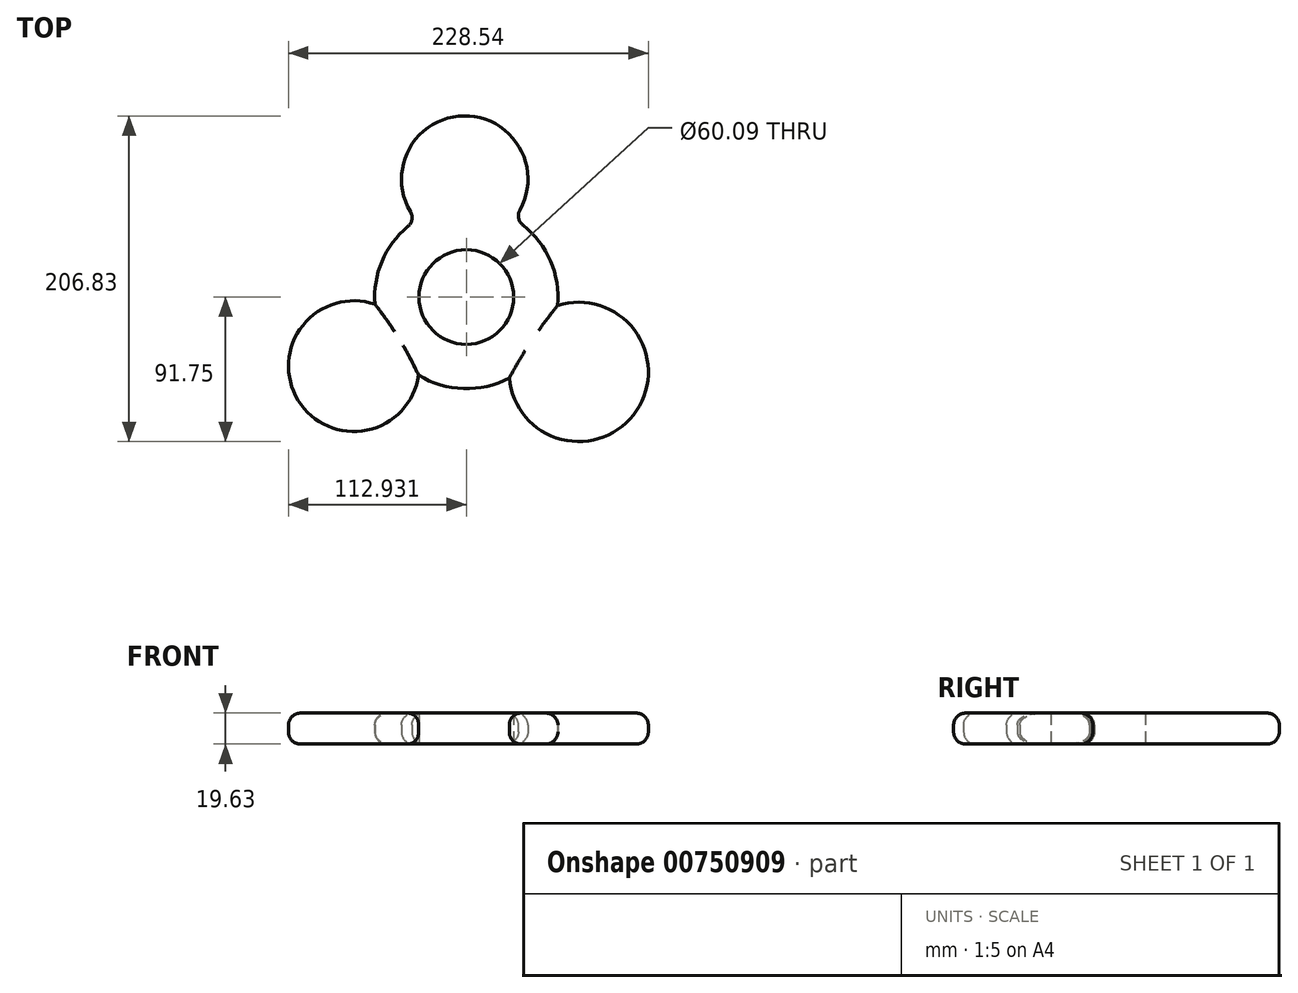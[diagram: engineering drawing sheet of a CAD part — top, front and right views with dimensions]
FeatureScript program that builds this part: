
annotation { "Feature Type Name" : "Feature", "Feature Type Description" : "" }
export const myFeature = defineFeature(function(context is Context, id is Id, definition is map)
    precondition{}
    {
        {
            var Q0;
            Q0=qCreatedBy(makeId("Top.planeOp"),FACE);
            var sketch = newSketch(context, id + "F0", { "sketchPlane" : qUnion([Q0])});
            skCircle(sketch, "E0", {"center": v(5.2, 0) * mm, "radius": 30.04 * mm});
            skCircle(sketch, "E1", {"center": v(5.2, 0) * mm, "radius": 58.18 * mm});
            skSolve(sketch);
        }
        {
            var Q0;
            Q0 = qSketchRegion(id + "F0", true);
            extrude(context, id + "F1", {"entities" : qUnion([Q0]), "depth" : 6.93 * mm, "offsetDistance" : 25.4 * mm});
        }
        {
            var Q0;
            Q0=qCreatedBy(makeId("Top.planeOp"),FACE);
            var sketch = newSketch(context, id + "F2", { "sketchPlane" : qUnion([Q0])});
            skCircle(sketch, "E2", {"center": v(4.18, 74.93) * mm, "radius": 40.15 * mm});
            skCircle(sketch, "E3", {"center": v(-66.22, -43.86) * mm, "radius": 41.52 * mm});
            skCircle(sketch, "E4", {"center": v(76.59, -47.53) * mm, "radius": 44.23 * mm});
            skSolve(sketch);
        }
        {
            var Q0;
            Q0 = qSketchRegion(id + "F2", true);
            extrude(context, id + "F3", {"entities" : qUnion([Q0]), "operationType" : NewBodyOperationType.ADD, "depth" : 6.93 * mm, "offsetDistance" : 25.4 * mm});
        }
        {
            var Q0;
            Q0=makeQuery(id+"F3.boolean.opBoolean","MERGE",FACE,{"derivedFrom":[makeQuery(id+"F1.opExtrude","CAP_FACE",FACE,{"disambiguationData":[OSD([sQuery(id+"F0.wireOp",EDGE,"E0"),sQuery(id+"F0.wireOp",EDGE,"E1")])],"isStart":false}),makeQuery(id+"F3.opExtrude","CAP_FACE",FACE,{"disambiguationData":[OSD([sQuery(id+"F2.wireOp",EDGE,"E2"),sQuery(id+"F2.wireOp",EDGE,"RJi2fS6J-4N5A-JJYD-STQZ-maYoIMxHux2H")])],"isStart":false}),makeQuery(id+"F3.opExtrude","CAP_FACE",FACE,{"disambiguationData":[OSD([sQuery(id+"F2.wireOp",EDGE,"E3"),sQuery(id+"F2.wireOp",EDGE,"9FHdYVCZ-X2J7-zCW8-irfW-GTTB5p2rgJZV")])],"isStart":false}),makeQuery(id+"F3.opExtrude","CAP_FACE",FACE,{"disambiguationData":[OSD([sQuery(id+"F2.wireOp",EDGE,"E4"),sQuery(id+"F2.wireOp",EDGE,"hhuE4voa-zWzk-uKp9-sCeD-eiZH0AJFDme7")])],"isStart":false})]});
            extrude(context, id + "F4", {"entities" : qUnion([Q0]), "operationType" : NewBodyOperationType.ADD, "depth" : 12.7 * mm, "offsetDistance" : 25.4 * mm});
        }
        {
            var Q0;
            {var subQ0=sQuery(id+"F2.wireOp",EDGE,"E3");var subQ1=sQuery(id+"F0.wireOp",EDGE,"E1");var subQ2=sQuery(id+"F2.wireOp",EDGE,"E4");Q0=makeQuery(id+"F4.opExtrude","CAP_EDGE",EDGE,{"disambiguationData":[OSD([subQ1]),TDD([makeQuery(id+"F3.boolean.opBoolean","SPLIT",EDGE,{"disambiguationData":[TD([makeQuery(id+"F1.opExtrude","CAP_FACE",FACE,{"disambiguationData":[OSD([sQuery(id+"F0.wireOp",EDGE,"E0"),subQ1])],"isStart":false}),makeQuery(id+"F1.opExtrude","SWEPT_FACE",FACE,{"disambiguationData":[OSD([subQ1])]}),makeQuery(id+"F3.opExtrude","CAP_FACE",FACE,{"disambiguationData":[OSD([sQuery(id+"F2.wireOp",EDGE,"E2"),sQuery(id+"F2.wireOp",EDGE,"RJi2fS6J-4N5A-JJYD-STQZ-maYoIMxHux2H")])],"isStart":false}),makeQuery(id+"F3.opExtrude","SWEPT_FACE",FACE,{"disambiguationData":[OSD([subQ0])]}),makeQuery(id+"F3.opExtrude","CAP_FACE",FACE,{"disambiguationData":[OSD([subQ0,sQuery(id+"F2.wireOp",EDGE,"9FHdYVCZ-X2J7-zCW8-irfW-GTTB5p2rgJZV")])],"isStart":false}),makeQuery(id+"F3.opExtrude","SWEPT_FACE",FACE,{"disambiguationData":[OSD([subQ2])]}),makeQuery(id+"F3.opExtrude","CAP_FACE",FACE,{"disambiguationData":[OSD([subQ2,sQuery(id+"F2.wireOp",EDGE,"hhuE4voa-zWzk-uKp9-sCeD-eiZH0AJFDme7")])],"isStart":false})])],"derivedFrom":makeQuery(id+"F1.opExtrude","CAP_EDGE",EDGE,{"disambiguationData":[OSD([subQ1])],"isStart":false})})])],"isStart":false});}
            var Q1;
            {var subQ0=sQuery(id+"F0.wireOp",EDGE,"E1");var subQ1=sQuery(id+"F2.wireOp",EDGE,"E3");var subQ2=sQuery(id+"F2.wireOp",EDGE,"E4");Q1=makeQuery(id+"F3.boolean.opBoolean","SPLIT",EDGE,{"disambiguationData":[TD([makeQuery(id+"F1.opExtrude","CAP_FACE",FACE,{"disambiguationData":[OSD([sQuery(id+"F0.wireOp",EDGE,"E0"),subQ0])],"isStart":true}),makeQuery(id+"F1.opExtrude","SWEPT_FACE",FACE,{"disambiguationData":[OSD([subQ0])]}),makeQuery(id+"F3.opExtrude","CAP_FACE",FACE,{"disambiguationData":[OSD([sQuery(id+"F2.wireOp",EDGE,"E2"),sQuery(id+"F2.wireOp",EDGE,"RJi2fS6J-4N5A-JJYD-STQZ-maYoIMxHux2H")])],"isStart":true}),makeQuery(id+"F3.opExtrude","SWEPT_FACE",FACE,{"disambiguationData":[OSD([subQ1])]}),makeQuery(id+"F3.opExtrude","CAP_FACE",FACE,{"disambiguationData":[OSD([subQ1,sQuery(id+"F2.wireOp",EDGE,"9FHdYVCZ-X2J7-zCW8-irfW-GTTB5p2rgJZV")])],"isStart":true}),makeQuery(id+"F3.opExtrude","SWEPT_FACE",FACE,{"disambiguationData":[OSD([subQ2])]}),makeQuery(id+"F3.opExtrude","CAP_FACE",FACE,{"disambiguationData":[OSD([subQ2,sQuery(id+"F2.wireOp",EDGE,"hhuE4voa-zWzk-uKp9-sCeD-eiZH0AJFDme7")])],"isStart":true})])],"derivedFrom":makeQuery(id+"F1.opExtrude","CAP_EDGE",EDGE,{"disambiguationData":[OSD([subQ0])],"isStart":true})});}
            var Q2;
            Q2=makeQuery(id+"F4.opExtrude","CAP_EDGE",EDGE,{"disambiguationData":[OSD([sQuery(id+"F2.wireOp",EDGE,"E4")])],"isStart":false});
            var Q3;
            Q3=makeQuery(id+"F3.opExtrude","CAP_EDGE",EDGE,{"disambiguationData":[OSD([sQuery(id+"F2.wireOp",EDGE,"E4")])],"isStart":true});
            var Q4;
            {var subQ0=sQuery(id+"F2.wireOp",EDGE,"E2");var subQ1=sQuery(id+"F0.wireOp",EDGE,"E1");var subQ2=sQuery(id+"F2.wireOp",EDGE,"E4");Q4=makeQuery(id+"F4.opExtrude","CAP_EDGE",EDGE,{"disambiguationData":[OSD([subQ1]),TDD([makeQuery(id+"F3.boolean.opBoolean","SPLIT",EDGE,{"disambiguationData":[TD([makeQuery(id+"F1.opExtrude","CAP_FACE",FACE,{"disambiguationData":[OSD([sQuery(id+"F0.wireOp",EDGE,"E0"),subQ1])],"isStart":false}),makeQuery(id+"F1.opExtrude","SWEPT_FACE",FACE,{"disambiguationData":[OSD([subQ1])]}),makeQuery(id+"F3.opExtrude","SWEPT_FACE",FACE,{"disambiguationData":[OSD([subQ0])]}),makeQuery(id+"F3.opExtrude","CAP_FACE",FACE,{"disambiguationData":[OSD([subQ0,sQuery(id+"F2.wireOp",EDGE,"RJi2fS6J-4N5A-JJYD-STQZ-maYoIMxHux2H")])],"isStart":false}),makeQuery(id+"F3.opExtrude","CAP_FACE",FACE,{"disambiguationData":[OSD([sQuery(id+"F2.wireOp",EDGE,"E3"),sQuery(id+"F2.wireOp",EDGE,"9FHdYVCZ-X2J7-zCW8-irfW-GTTB5p2rgJZV")])],"isStart":false}),makeQuery(id+"F3.opExtrude","SWEPT_FACE",FACE,{"disambiguationData":[OSD([subQ2])]}),makeQuery(id+"F3.opExtrude","CAP_FACE",FACE,{"disambiguationData":[OSD([subQ2,sQuery(id+"F2.wireOp",EDGE,"hhuE4voa-zWzk-uKp9-sCeD-eiZH0AJFDme7")])],"isStart":false})])],"derivedFrom":makeQuery(id+"F1.opExtrude","CAP_EDGE",EDGE,{"disambiguationData":[OSD([subQ1])],"isStart":false})})])],"isStart":false});}
            var Q5;
            Q5=makeQuery(id+"F4.opExtrude","CAP_EDGE",EDGE,{"disambiguationData":[OSD([sQuery(id+"F2.wireOp",EDGE,"E2")])],"isStart":false});
            var Q6;
            {var subQ0=sQuery(id+"F2.wireOp",EDGE,"E2");var subQ1=sQuery(id+"F0.wireOp",EDGE,"E1");var subQ2=sQuery(id+"F2.wireOp",EDGE,"E3");Q6=makeQuery(id+"F4.opExtrude","CAP_EDGE",EDGE,{"disambiguationData":[OSD([subQ1]),TDD([makeQuery(id+"F3.boolean.opBoolean","SPLIT",EDGE,{"disambiguationData":[TD([makeQuery(id+"F1.opExtrude","CAP_FACE",FACE,{"disambiguationData":[OSD([sQuery(id+"F0.wireOp",EDGE,"E0"),subQ1])],"isStart":false}),makeQuery(id+"F1.opExtrude","SWEPT_FACE",FACE,{"disambiguationData":[OSD([subQ1])]}),makeQuery(id+"F3.opExtrude","SWEPT_FACE",FACE,{"disambiguationData":[OSD([subQ0])]}),makeQuery(id+"F3.opExtrude","CAP_FACE",FACE,{"disambiguationData":[OSD([subQ0,sQuery(id+"F2.wireOp",EDGE,"RJi2fS6J-4N5A-JJYD-STQZ-maYoIMxHux2H")])],"isStart":false}),makeQuery(id+"F3.opExtrude","SWEPT_FACE",FACE,{"disambiguationData":[OSD([subQ2])]}),makeQuery(id+"F3.opExtrude","CAP_FACE",FACE,{"disambiguationData":[OSD([subQ2,sQuery(id+"F2.wireOp",EDGE,"9FHdYVCZ-X2J7-zCW8-irfW-GTTB5p2rgJZV")])],"isStart":false}),makeQuery(id+"F3.opExtrude","CAP_FACE",FACE,{"disambiguationData":[OSD([sQuery(id+"F2.wireOp",EDGE,"E4"),sQuery(id+"F2.wireOp",EDGE,"hhuE4voa-zWzk-uKp9-sCeD-eiZH0AJFDme7")])],"isStart":false})])],"derivedFrom":makeQuery(id+"F1.opExtrude","CAP_EDGE",EDGE,{"disambiguationData":[OSD([subQ1])],"isStart":false})})])],"isStart":false});}
            var Q7;
            Q7=makeQuery(id+"F4.opExtrude","CAP_EDGE",EDGE,{"disambiguationData":[OSD([sQuery(id+"F2.wireOp",EDGE,"E3")])],"isStart":false});
            var Q8;
            Q8=makeQuery(id+"F3.opExtrude","CAP_EDGE",EDGE,{"disambiguationData":[OSD([sQuery(id+"F2.wireOp",EDGE,"E3")])],"isStart":true});
            var Q9;
            {var subQ0=sQuery(id+"F2.wireOp",EDGE,"E2");var subQ1=sQuery(id+"F0.wireOp",EDGE,"E1");var subQ2=sQuery(id+"F2.wireOp",EDGE,"E3");Q9=makeQuery(id+"F3.boolean.opBoolean","SPLIT",EDGE,{"disambiguationData":[TD([makeQuery(id+"F1.opExtrude","CAP_FACE",FACE,{"disambiguationData":[OSD([sQuery(id+"F0.wireOp",EDGE,"E0"),subQ1])],"isStart":true}),makeQuery(id+"F1.opExtrude","SWEPT_FACE",FACE,{"disambiguationData":[OSD([subQ1])]}),makeQuery(id+"F3.opExtrude","SWEPT_FACE",FACE,{"disambiguationData":[OSD([subQ0])]}),makeQuery(id+"F3.opExtrude","CAP_FACE",FACE,{"disambiguationData":[OSD([subQ0,sQuery(id+"F2.wireOp",EDGE,"RJi2fS6J-4N5A-JJYD-STQZ-maYoIMxHux2H")])],"isStart":true}),makeQuery(id+"F3.opExtrude","SWEPT_FACE",FACE,{"disambiguationData":[OSD([subQ2])]}),makeQuery(id+"F3.opExtrude","CAP_FACE",FACE,{"disambiguationData":[OSD([subQ2,sQuery(id+"F2.wireOp",EDGE,"9FHdYVCZ-X2J7-zCW8-irfW-GTTB5p2rgJZV")])],"isStart":true}),makeQuery(id+"F3.opExtrude","CAP_FACE",FACE,{"disambiguationData":[OSD([sQuery(id+"F2.wireOp",EDGE,"E4"),sQuery(id+"F2.wireOp",EDGE,"hhuE4voa-zWzk-uKp9-sCeD-eiZH0AJFDme7")])],"isStart":true})])],"derivedFrom":makeQuery(id+"F1.opExtrude","CAP_EDGE",EDGE,{"disambiguationData":[OSD([subQ1])],"isStart":true})});}
            var Q10;
            {var subQ0=sQuery(id+"F2.wireOp",EDGE,"E2");Q10=makeQuery(id+"F4.boolean.opBoolean","MERGE",FACE,{"derivedFrom":[makeQuery(id+"F3.opExtrude","SWEPT_FACE",FACE,{"disambiguationData":[OSD([subQ0])]}),makeQuery(id+"F4.opExtrude","SWEPT_FACE",FACE,{"disambiguationData":[OSD([subQ0])]})]});}
            var Q11;
            {var subQ0=sQuery(id+"F2.wireOp",EDGE,"E2");var subQ1=sQuery(id+"F0.wireOp",EDGE,"E1");var subQ2=sQuery(id+"F2.wireOp",EDGE,"E4");Q11=makeQuery(id+"F3.boolean.opBoolean","SPLIT",EDGE,{"disambiguationData":[TD([makeQuery(id+"F1.opExtrude","CAP_FACE",FACE,{"disambiguationData":[OSD([sQuery(id+"F0.wireOp",EDGE,"E0"),subQ1])],"isStart":true}),makeQuery(id+"F1.opExtrude","SWEPT_FACE",FACE,{"disambiguationData":[OSD([subQ1])]}),makeQuery(id+"F3.opExtrude","SWEPT_FACE",FACE,{"disambiguationData":[OSD([subQ0])]}),makeQuery(id+"F3.opExtrude","CAP_FACE",FACE,{"disambiguationData":[OSD([subQ0,sQuery(id+"F2.wireOp",EDGE,"RJi2fS6J-4N5A-JJYD-STQZ-maYoIMxHux2H")])],"isStart":true}),makeQuery(id+"F3.opExtrude","CAP_FACE",FACE,{"disambiguationData":[OSD([sQuery(id+"F2.wireOp",EDGE,"E3"),sQuery(id+"F2.wireOp",EDGE,"9FHdYVCZ-X2J7-zCW8-irfW-GTTB5p2rgJZV")])],"isStart":true}),makeQuery(id+"F3.opExtrude","SWEPT_FACE",FACE,{"disambiguationData":[OSD([subQ2])]}),makeQuery(id+"F3.opExtrude","CAP_FACE",FACE,{"disambiguationData":[OSD([subQ2,sQuery(id+"F2.wireOp",EDGE,"hhuE4voa-zWzk-uKp9-sCeD-eiZH0AJFDme7")])],"isStart":true})])],"derivedFrom":makeQuery(id+"F1.opExtrude","CAP_EDGE",EDGE,{"disambiguationData":[OSD([subQ1])],"isStart":true})});}
            fillet(context, id + "F5", {"entities" : qUnion([Q0, Q1, Q2, Q3, Q4, Q5, Q6, Q7, Q8, Q9, Q10, Q11]), "radius" : 7.62 * mm, "tangentPropagation" : true, "allowEdgeOverflow" : false});
        }
    });
